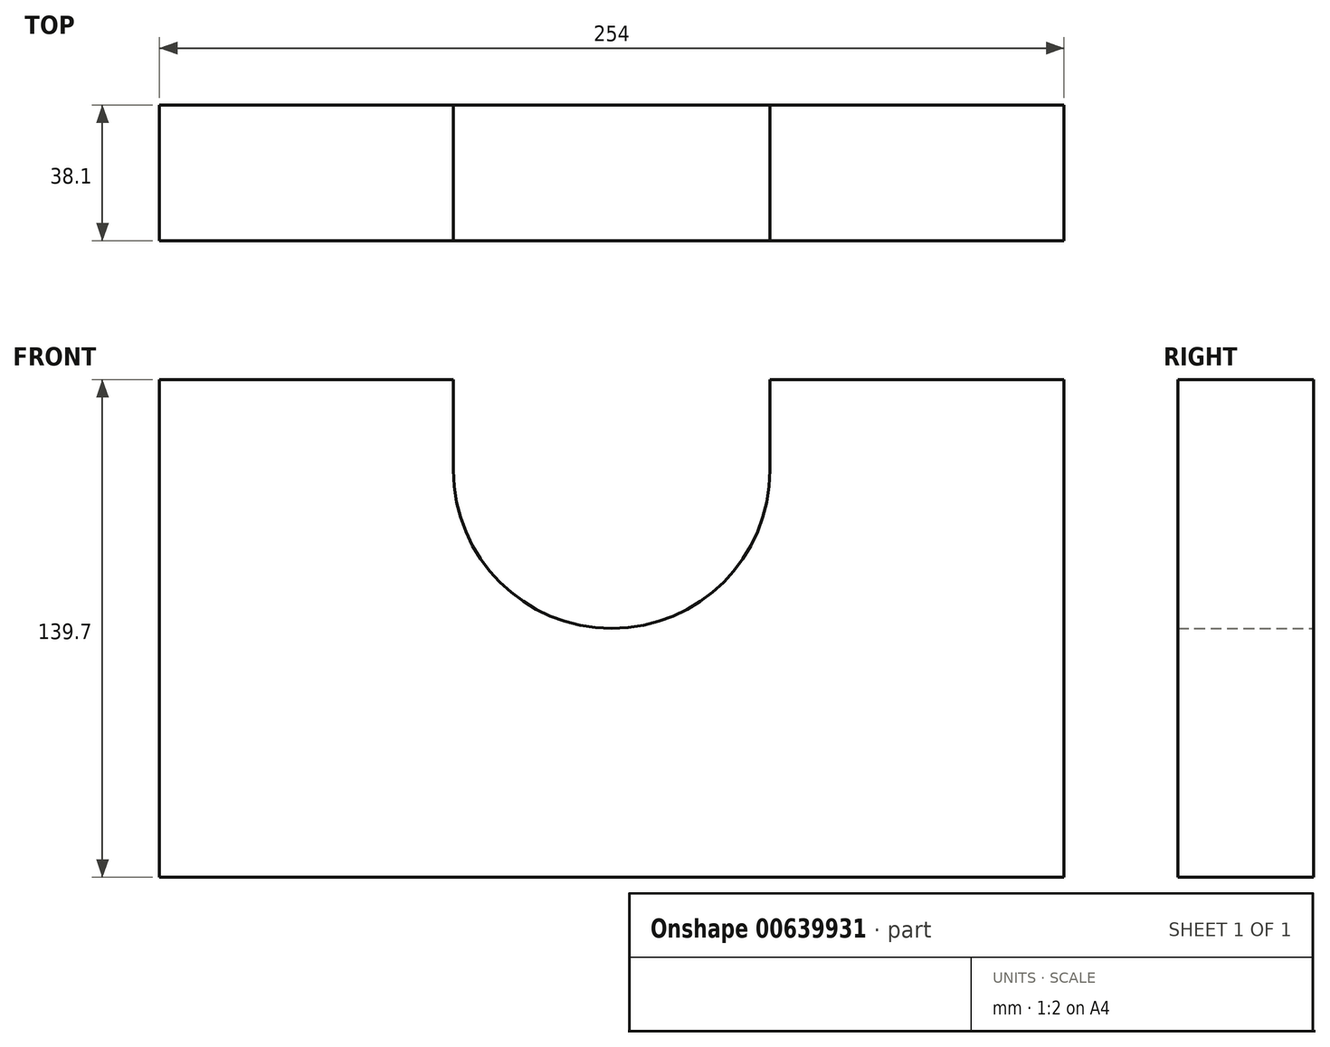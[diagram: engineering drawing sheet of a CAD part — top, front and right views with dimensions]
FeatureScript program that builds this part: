
annotation { "Feature Type Name" : "Feature", "Feature Type Description" : "" }
export const myFeature = defineFeature(function(context is Context, id is Id, definition is map)
    precondition{}
    {
        {
            var Q0;
            Q0=qCreatedBy(makeId("Front.planeOp"),FACE);
            var sketch = newSketch(context, id + "F0", { "sketchPlane" : qUnion([Q0])});
            skLineSegment(sketch, "E0.bottom", {"start": v(0, 0) * mm, "end": v(254, 0) * mm});
            skLineSegment(sketch, "E0.top", {"start": v(0, 139.7) * mm, "end": v(82.55, 139.7) * mm});
            skLineSegment(sketch, "E0.left", {"start": v(0, 0) * mm, "end": v(0, 139.7) * mm});
            skLineSegment(sketch, "E0.right", {"start": v(254, 0) * mm, "end": v(254, 139.7) * mm});
            skLineSegment(sketch, "E1.trimOffspring", {"start": v(171.45, 139.7) * mm, "end": v(254, 139.7) * mm});
            skLineSegment(sketch, "E2", {"start": v(171.45, 139.7) * mm, "end": v(171.45, 114.3) * mm});
            skLineSegment(sketch, "E3", {"start": v(82.55, 139.7) * mm, "end": v(82.55, 114.3) * mm});
            skArc(sketch, "E4", {"start": v(82.55, 114.3) * mm, "mid": v(127, 69.85) * mm, "end": v(171.45, 114.3) * mm});
            skSolve(sketch);
        }
        {
            var Q0;
            Q0=makeQuery(id+"F0.imprint","IMPRINT",FACE,{"disambiguationData":[TD([[makeQuery(id+"F0.imprint","IMPRINT",EDGE,{"derivedFrom":sQuery(id+"F0.wireOp",EDGE,"E0.bottom")}),1.0]])]});
            extrude(context, id + "F1", {"entities" : qUnion([Q0]), "depth" : 38.1 * mm, "offsetDistance" : 25.4 * mm});
        }
    });
